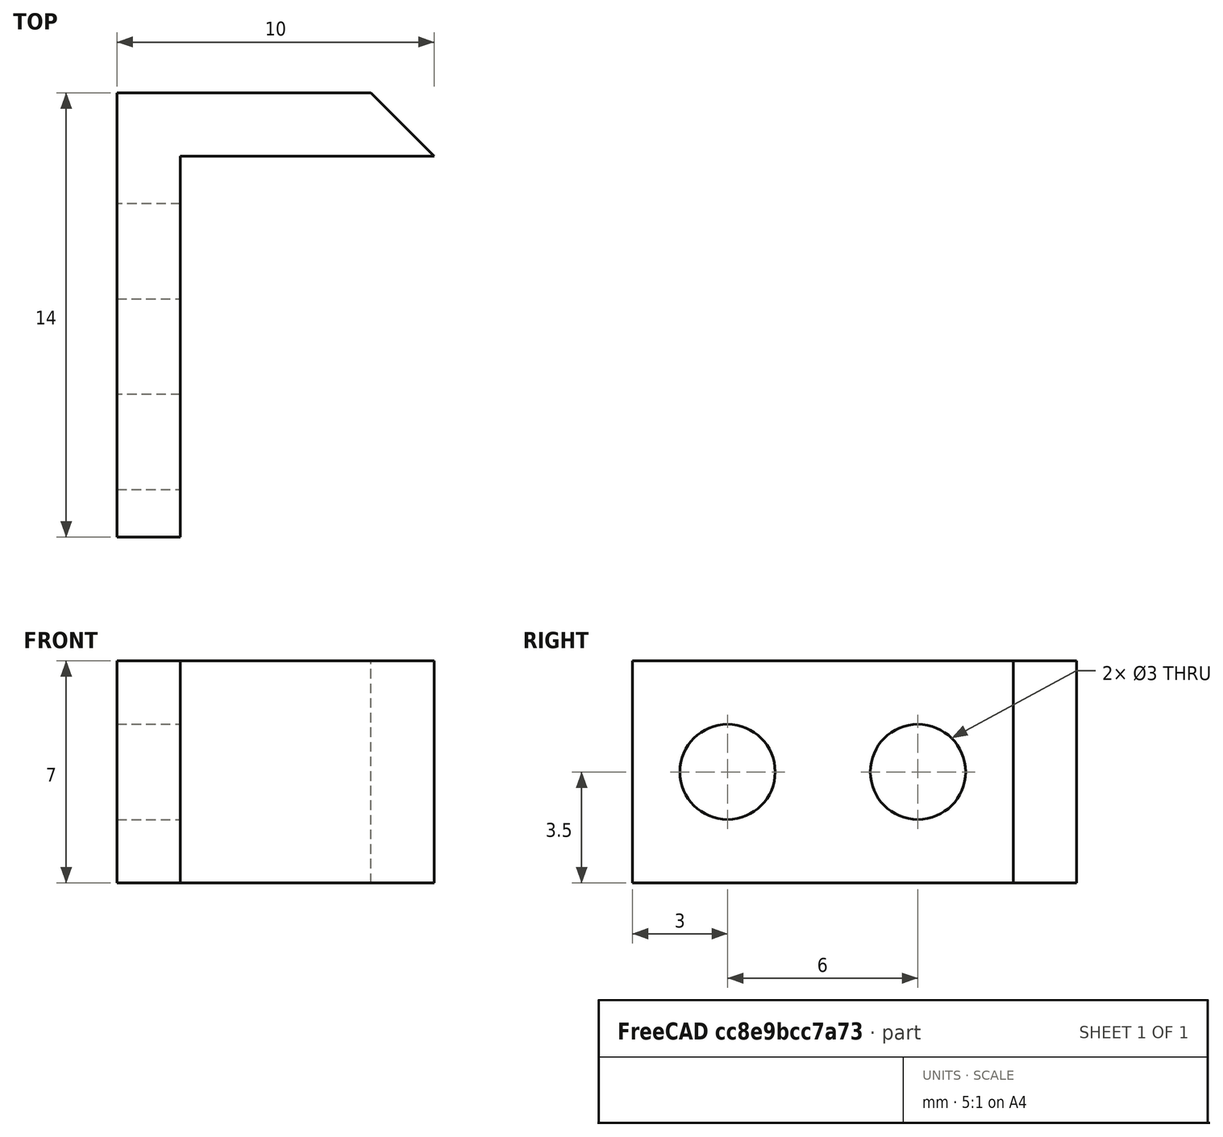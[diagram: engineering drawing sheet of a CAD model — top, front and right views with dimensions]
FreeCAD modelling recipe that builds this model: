
FCSTD DOCUMENT  (FreeCAD 0.18.4R)
Label: 19
License: All rights reserved
LicenseURL: http://en.wikipedia.org/wiki/All_rights_reserved
objects: Sketcher::SketchObject×2, PartDesign::Pad×1, PartDesign::Pocket×1, PartDesign::Body×1
note: 7 computed .brp shape members not serialized (recipe doc carries the construction recipe); baked Part::Feature solids carry a one-line shape summary decoded from their .brp

FEATURE [Sketcher::SketchObject] Sketch  label="Unnamed"
  constraints (17):
    c: Coincident(g0,g1)
    c: Horizontal(g0)
    c: Vertical(g1)
    c: Coincident(g0,g-1)
    c: Coincident(g2,g3)
    c: Coincident(g3,g4)
    c: Coincident(g4,g5)
    c: Horizontal(g2)
    c: Horizontal(g4)
    c: Vertical(g5)
    c: Distance(g0) = 2
    c: Distance(g5) = 14
    c: Coincident(g5,g0)
    c: Coincident(g2,g1)
    c: Angle(g3,g2) = 0.785398
    c: Distance(g3,g2) = 2
    c: Distance(g2,g5) = 10
FEATURE [PartDesign::Pad] Pad  label="Unnamed"
  Length = 100
  Length2 = 100
  Type = 0
FEATURE [Sketcher::SketchObject] Sketch001  label="Unnamed"
FEATURE [PartDesign::Pocket] Pocket  label="Unnamed"
  Length = 100
  Length2 = 100
  Type = 0
FEATURE [PartDesign::Body] Body
  Group = -> [Sketch,Pad,Sketch001,Pocket]
  Origin = -> Origin
  Tip = -> Pocket
